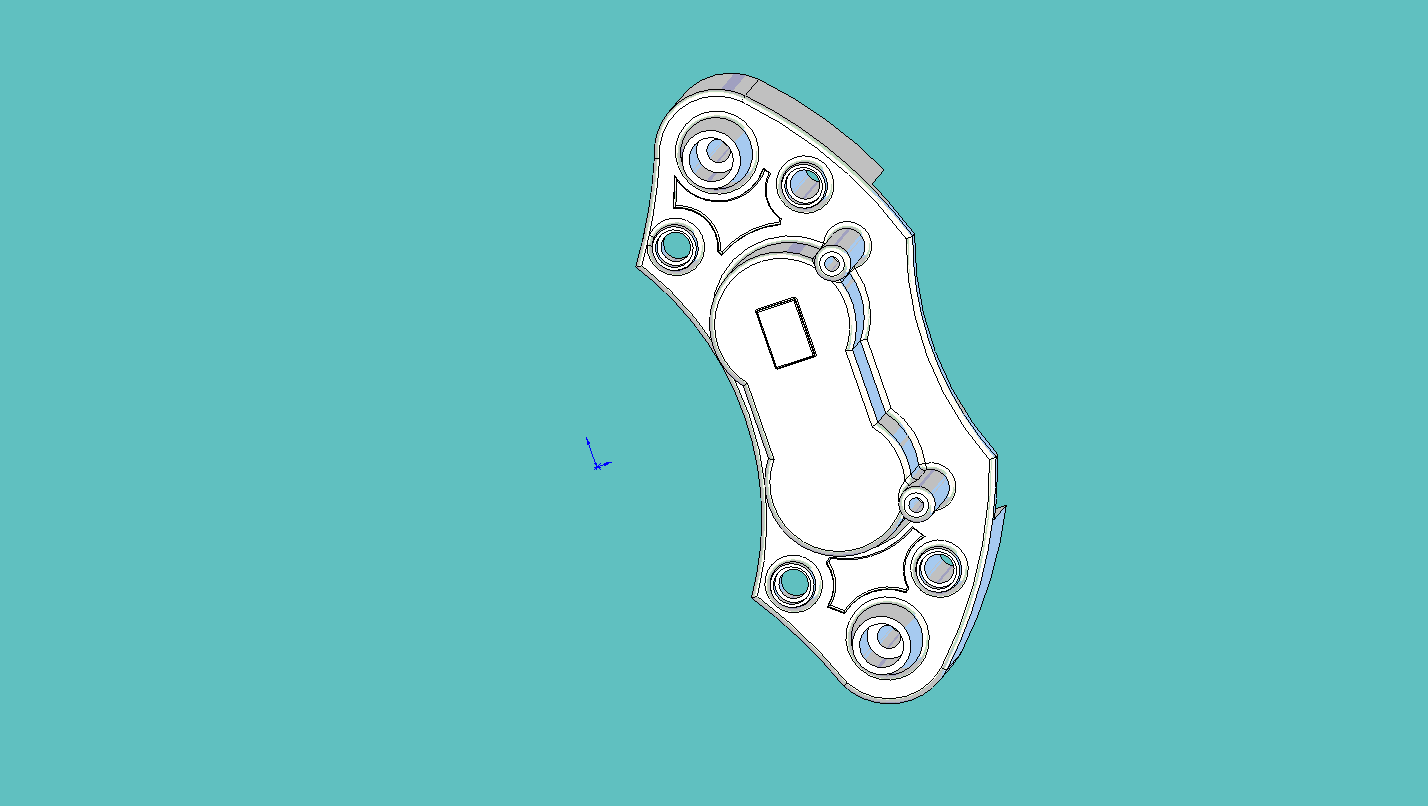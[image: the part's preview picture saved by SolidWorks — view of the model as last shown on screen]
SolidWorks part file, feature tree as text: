
SOLIDWORKS PART (.sldprt)
format: sldprt  version: not decoded by parser v0  size: 1,540,096 bytes
history: native  units: mm
features: sketch x17, cut_extrude x11, fillet x9, extrude x6, plane x2, material x1, chamfer x1 (+13 scaffold rows collapsed)
feature tree (60):
  scaffold x13  (default folders/planes/origin — collapsed)
  material  "Material <not specified>"
  sketch  "Sketch1"  dims[D1=63.5mm]
  extrude  "Extrude1"  Depth=31.75mm
  sketch  "Sketch5"  dims[D1=~43.962388mm]
  extrude  "Extrude2"  Depth=50.8mm
  sketch  "Sketch3"  dims[D1=50.0mm]
  cut_extrude  "Cut-Extrude1"  Depth=25.4mm
  sketch  "Sketch7"  dims[c1.D1=12.7mm c1.D2=12.7mm c2.D1=~13.906952mm c2.D2=25.0mm c2.D3=25.0mm c3.D1=~12.799272mm c3.D3=~153.706634mm]
  fillet  "Fillet1"  Radius=2.54mm
  fillet  "Fillet2"  Radius=2.54mm
  fillet  "Fillet3"  Radius=2.54mm
  sketch  "Sketch10"
  cut_extrude  "Cut-Extrude3"  [1 undecoded]
  plane  "Plane1"  Offset=10.16mm
  plane  "Plane2"  Offset=8.636mm
  sketch  "Sketch13"  dims[D1=273.05mm D2=137.16mm]
  cut_extrude  "Cut-Extrude4"  [1 undecoded]
  sketch  "Sketch14"
  cut_extrude  "Cut-Extrude5"  [1 undecoded]
  sketch  "Sketch15"
  extrude  "Extrude3"  Depth=53.18mm
  fillet  "Fillet4"  Radius=2.54mm
  sketch  "Sketch16"  dims[D1=~1.636236mm]
  cut_extrude  "Cut-Extrude6"  Depth=27.94mm
  fillet  "Fillet5"  Radius=2.54mm
  sketch  "Sketch17"
  extrude  "Extrude4"  Depth=2.54mm
  fillet  "Fillet6"  Radius=0.508mm
  chamfer  "Chamfer1"  Distance=1.27mm Angle=45deg
  sketch  "Sketch20"  dims[c1.D1=31.75mm c1.D2=25.4mm c2.D1=~20.003376mm]
  extrude  "Extrude5"  Depth=20.32mm
  cut_extrude  "Cut-Extrude8"  [1 undecoded]
  sketch  "Sketch21"  dims[D1=~4.108238mm]
  cut_extrude  "Cut-Extrude10"  Depth=25.4mm
  fillet  "Fillet7"  Radius=2.54mm
  sketch  "Sketch22"  dims[D1=10.16mm]
  cut_extrude  "Cut-Extrude11"  [1 undecoded]
  sketch  "Sketch24"
  cut_extrude  "Cut-Extrude12"  Depth=22.86mm
  sketch  "Sketch25"  dims[D1=20.574mm]
  extrude  "Extrude6"  Depth=5.08mm
  fillet  "Fillet8"  Radius=2.54mm
  sketch  "Sketch27"  dims[D1=~16.253517mm]
  cut_extrude  "Cut-Extrude15"  Depth=5.08mm
  sketch  "Sketch28"
  cut_extrude  "Cut-Extrude16"  Depth=2.54mm
  fillet  "Fillet9"  Radius=0.762mm
decode coverage: 33 of 44 modeling features carry decoded parameters
note: ~ marks probable driven/reference dimensions
note: 5 parameter values undecoded
summary: no parameter record found for 5 features
note: suppression state not decoded; provenance and decode notes live in map.json
